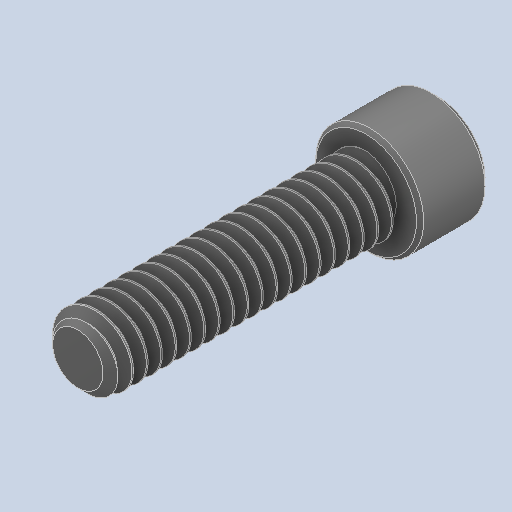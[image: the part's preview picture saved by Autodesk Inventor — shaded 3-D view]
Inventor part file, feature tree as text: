
AUTODESK INVENTOR PART (.ipt)
format: ipt  version: 2024.2 (Build 282272000, 272)  size: 709,120 bytes
history: native  units: in
note: dims shown in document units (in); Inventor stores cm internally (conversion verified against a paired STEP export)
features: chamfer x1
ambient origin geometry x8: Origin, YZ Plane, XZ Plane, XY Plane, X Axis, Y Axis, Z Axis, Center Point
bodies: Solid1 (feature_tree)
feature tree (1):
  chamfer  "Chamfer2"  [1 undecoded]
note: 1 required parameter value undecoded (feature->parameter linkage not recoverable at this tier; creation-order binding heuristic only, values carry confidence <= 0.55)
